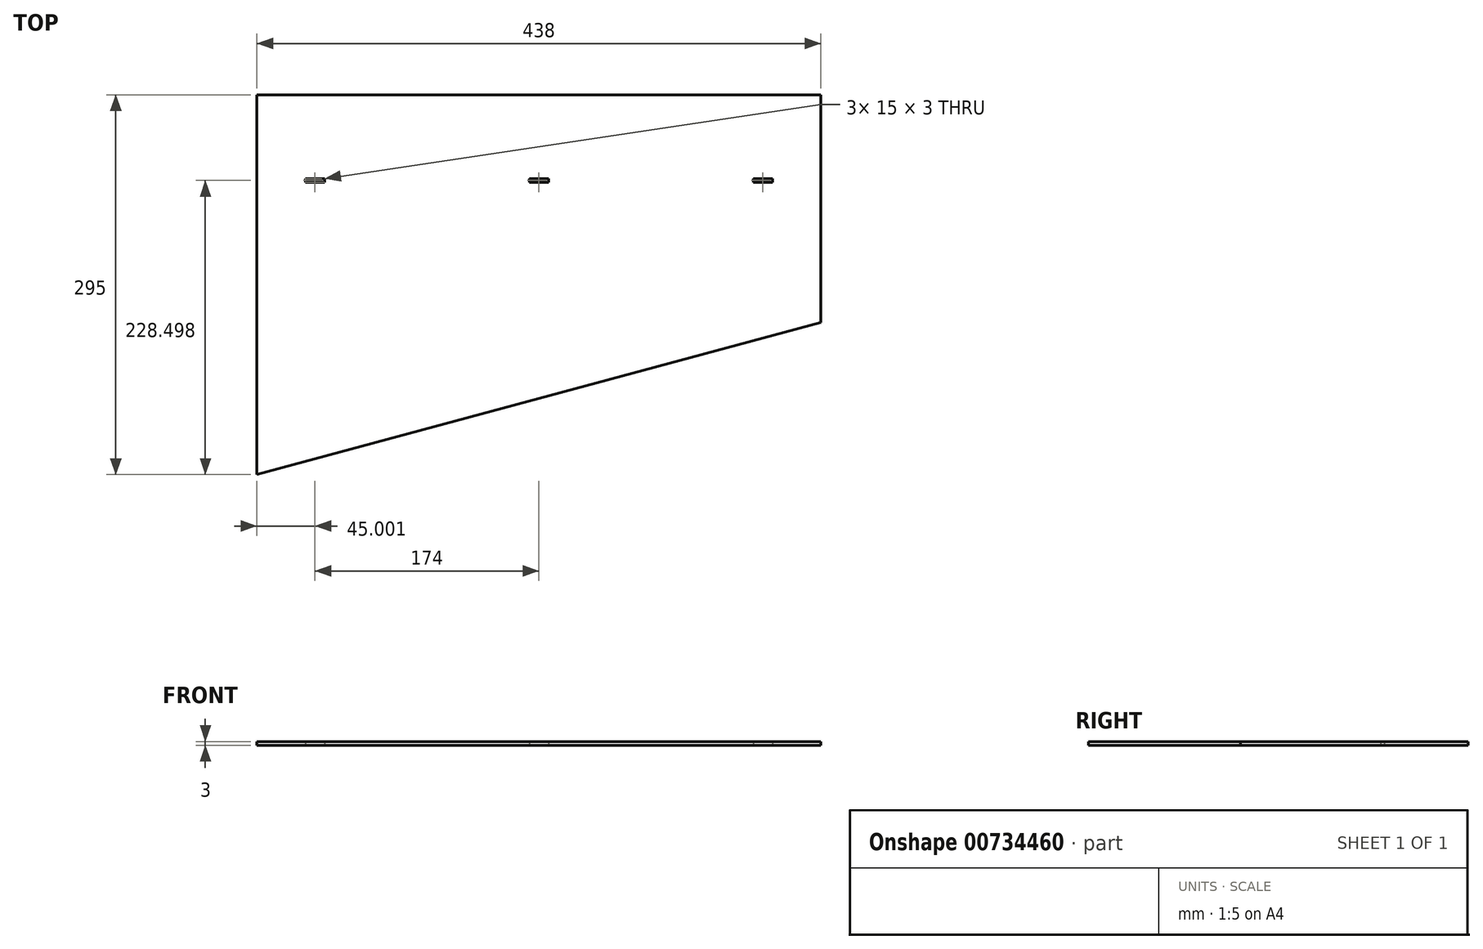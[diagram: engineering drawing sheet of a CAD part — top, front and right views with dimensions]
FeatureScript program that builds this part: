
annotation { "Feature Type Name" : "Feature", "Feature Type Description" : "" }
export const myFeature = defineFeature(function(context is Context, id is Id, definition is map)
    precondition{}
    {
        {
            var Q0;
            Q0=qCreatedBy(makeId("Top.planeOp"),FACE);
            var sketch = newSketch(context, id + "F0", { "sketchPlane" : qUnion([Q0])});
            skLineSegment(sketch, "E0", {"start": v(-185.79, 212.46) * mm, "end": v(-185.79, -82.54) * mm});
            skLineSegment(sketch, "E1", {"start": v(-185.79, 212.46) * mm, "end": v(252.21, 212.46) * mm});
            skLineSegment(sketch, "E2", {"start": v(252.21, 212.46) * mm, "end": v(252.21, 35.46) * mm});
            skLineSegment(sketch, "E3", {"start": v(252.21, 35.46) * mm, "end": v(-185.79, -82.54) * mm});
            skLineSegment(sketch, "E4.bottom", {"start": v(214.71, 144.46) * mm, "end": v(199.71, 144.46) * mm});
            skLineSegment(sketch, "E4.top", {"start": v(214.71, 147.46) * mm, "end": v(199.71, 147.46) * mm});
            skLineSegment(sketch, "E4.left", {"start": v(214.71, 144.46) * mm, "end": v(214.71, 147.46) * mm});
            skLineSegment(sketch, "E4.right", {"start": v(-148.29, 144.46) * mm, "end": v(-148.29, 147.46) * mm});
            skLineSegment(sketch, "E5.bottom", {"start": v(-148.29, 147.46) * mm, "end": v(-133.29, 147.46) * mm});
            skLineSegment(sketch, "E5.top", {"start": v(-148.29, 144.46) * mm, "end": v(-133.29, 144.46) * mm});
            skLineSegment(sketch, "E5.left", {"start": v(-148.29, 147.46) * mm, "end": v(-148.29, 144.46) * mm});
            skLineSegment(sketch, "E5.right", {"start": v(-133.29, 147.46) * mm, "end": v(-133.29, 144.46) * mm});
            skLineSegment(sketch, "E6.bottom", {"start": v(25.71, 147.46) * mm, "end": v(40.71, 147.46) * mm});
            skLineSegment(sketch, "E6.top", {"start": v(25.71, 144.46) * mm, "end": v(40.71, 144.46) * mm});
            skLineSegment(sketch, "E6.left", {"start": v(25.71, 147.46) * mm, "end": v(25.71, 144.46) * mm});
            skLineSegment(sketch, "E6.right", {"start": v(40.71, 147.46) * mm, "end": v(40.71, 144.46) * mm});
            skLineSegment(sketch, "E7.left", {"start": v(214.71, 147.46) * mm, "end": v(214.71, 144.46) * mm});
            skLineSegment(sketch, "E7.right", {"start": v(199.71, 147.46) * mm, "end": v(199.71, 144.46) * mm});
            skLineSegment(sketch, "E8.trimOffspring", {"start": v(-133.29, 147.46) * mm, "end": v(-148.29, 147.46) * mm});
            skLineSegment(sketch, "E9.trimOffspring", {"start": v(-133.29, 144.46) * mm, "end": v(-148.29, 144.46) * mm});
            skLineSegment(sketch, "E10.trimOffspring", {"start": v(40.71, 144.46) * mm, "end": v(25.71, 144.46) * mm});
            skLineSegment(sketch, "E11.trimOffspring", {"start": v(40.71, 147.46) * mm, "end": v(25.71, 147.46) * mm});
            skSolve(sketch);
        }
        {
            var Q0;
            Q0=makeQuery(id+"F0.imprint","IMPRINT",FACE,{"disambiguationData":[TD([[makeQuery(id+"F0.imprint","IMPRINT",EDGE,{"derivedFrom":sQuery(id+"F0.wireOp",EDGE,"E0")}),1.0]])]});
            extrude(context, id + "F1", {"entities" : qUnion([Q0]), "depth" : 3 * mm});
        }
    });
